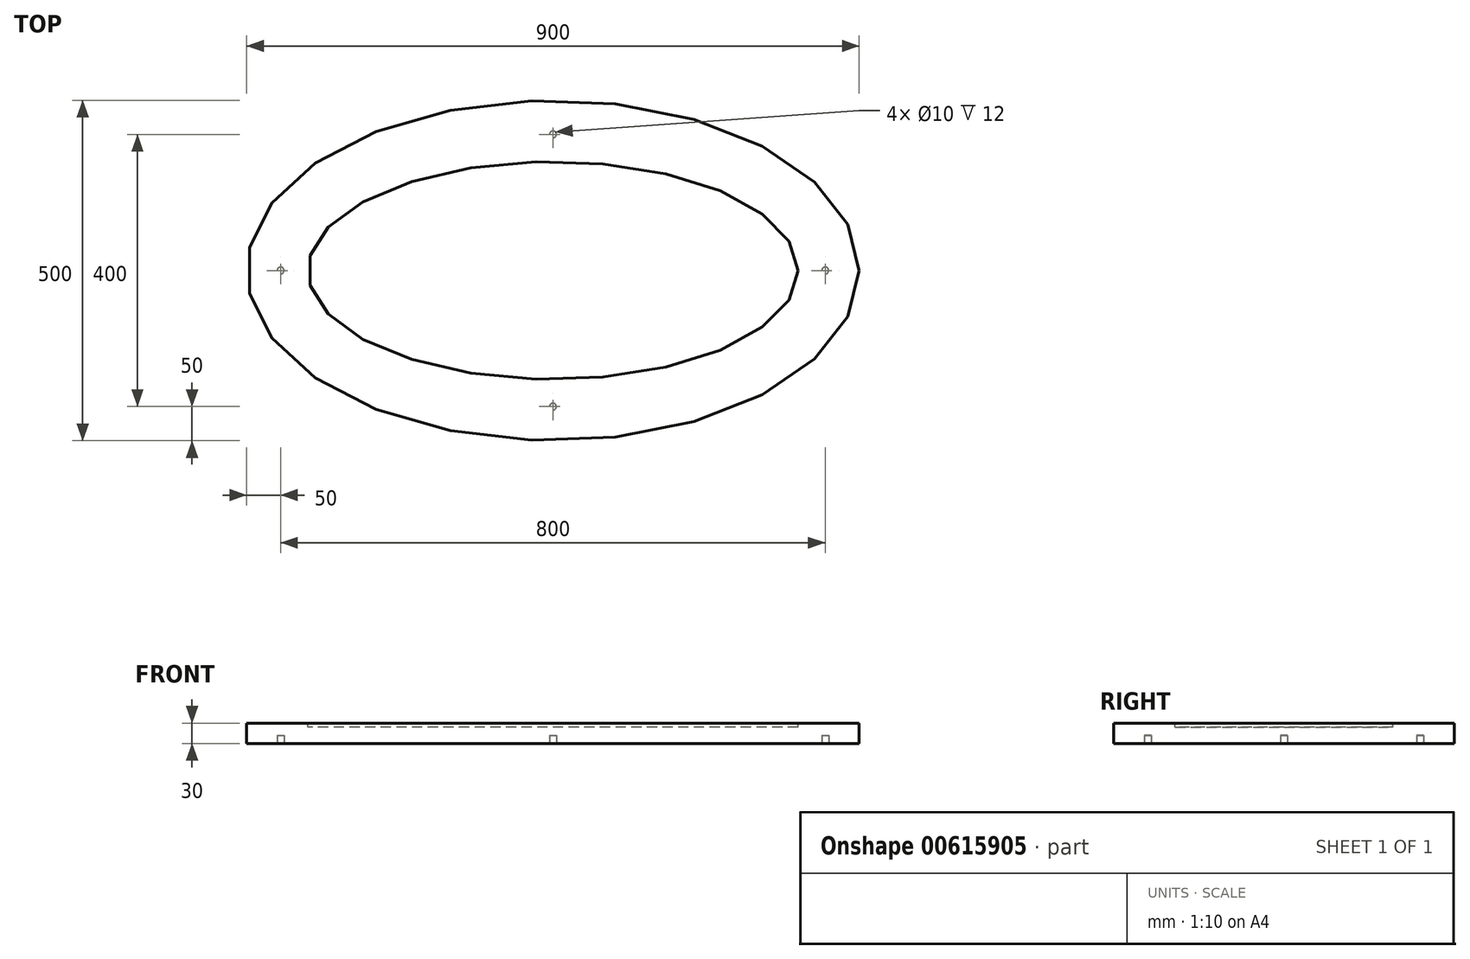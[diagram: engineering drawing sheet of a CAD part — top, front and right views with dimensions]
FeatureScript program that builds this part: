
annotation { "Feature Type Name" : "Feature", "Feature Type Description" : "" }
export const myFeature = defineFeature(function(context is Context, id is Id, definition is map)
    precondition{}
    {
        {
            var Q0;
            Q0=qCreatedBy(makeId("Top.planeOp"),FACE);
            var sketch = newSketch(context, id + "F0", { "sketchPlane" : qUnion([Q0])});
            skEllipse(sketch, "E0", {"center": v(0, 0) * mm, "majorRadius": 450 * mm, "minorRadius": 250 * mm, "majorAxis": v(1, 0)});
            skFitSpline(sketch, "E1.0", {"points": [v(349.97, -1.74) * mm, v(350.01, 0) * mm, v(349.97, 1.74) * mm, v(349.82, 4.08) * mm, v(349.42, 7.07) * mm, v(348.57, 10.9) * mm, v(347.27, 15.08) * mm, v(345.43, 19.64) * mm, v(342.94, 24.63) * mm, v(339.74, 30.04) * mm, v(335.72, 35.84) * mm, v(330.84, 41.98) * mm, v(325.03, 48.4) * mm, v(318.28, 55.05) * mm, v(310.55, 61.86) * mm, v(301.83, 68.75) * mm, v(293.75, 74.52) * mm, v(286.8, 79.12) * mm, v(281.33, 82.56) * mm, v(275.62, 85.98) * mm, v(269.67, 89.37) * mm, v(263.5, 92.72) * mm, v(257.12, 96) * mm, v(250.55, 99.23) * mm, v(241.54, 103.43) * mm, v(229.8, 108.51) * mm, v(215.03, 114.28) * mm, v(199.6, 119.7) * mm, v(178.22, 126.42) * mm, v(150.1, 133.81) * mm, v(120.4, 139.72) * mm, v(95.91, 143.5) * mm, v(77.2, 145.85) * mm, v(58.22, 147.69) * mm, v(42.2, 148.8) * mm, v(29.3, 149.42) * mm, v(19.56, 149.75) * mm, v(11.43, 149.92) * mm, v(4.9, 149.99) * mm, v(0, 150) * mm, v(-4.9, 149.99) * mm, v(-11.43, 149.92) * mm, v(-19.56, 149.75) * mm, v(-29.3, 149.42) * mm, v(-42.2, 148.8) * mm, v(-58.22, 147.69) * mm, v(-77.2, 145.85) * mm, v(-95.91, 143.5) * mm, v(-120.4, 139.72) * mm, v(-150.1, 133.81) * mm, v(-178.22, 126.42) * mm, v(-199.6, 119.7) * mm, v(-215.03, 114.28) * mm, v(-229.8, 108.51) * mm, v(-241.54, 103.43) * mm, v(-250.55, 99.23) * mm, v(-257.12, 96) * mm, v(-263.5, 92.72) * mm, v(-269.67, 89.37) * mm, v(-275.62, 85.98) * mm, v(-281.33, 82.56) * mm, v(-286.8, 79.12) * mm, v(-293.75, 74.52) * mm, v(-301.83, 68.75) * mm, v(-310.55, 61.86) * mm, v(-318.28, 55.05) * mm, v(-325.03, 48.4) * mm, v(-330.84, 41.98) * mm, v(-335.72, 35.84) * mm, v(-339.74, 30.04) * mm, v(-342.94, 24.63) * mm, v(-345.43, 19.64) * mm, v(-347.27, 15.08) * mm, v(-348.57, 10.9) * mm, v(-349.42, 7.07) * mm, v(-349.82, 4.08) * mm, v(-349.97, 1.74) * mm, v(-350.01, 0) * mm, v(-349.97, -1.74) * mm, v(-349.82, -4.08) * mm, v(-349.42, -7.07) * mm, v(-348.57, -10.9) * mm, v(-347.27, -15.08) * mm, v(-345.43, -19.64) * mm, v(-342.94, -24.63) * mm, v(-339.74, -30.04) * mm, v(-335.72, -35.84) * mm, v(-330.84, -41.98) * mm, v(-325.03, -48.4) * mm, v(-318.28, -55.05) * mm, v(-310.55, -61.86) * mm, v(-301.83, -68.75) * mm, v(-293.75, -74.52) * mm, v(-286.8, -79.12) * mm, v(-281.33, -82.56) * mm, v(-275.62, -85.98) * mm, v(-269.67, -89.37) * mm, v(-263.5, -92.72) * mm, v(-257.12, -96) * mm, v(-250.55, -99.23) * mm, v(-241.54, -103.43) * mm, v(-229.8, -108.51) * mm, v(-215.03, -114.28) * mm, v(-199.6, -119.7) * mm, v(-178.22, -126.42) * mm, v(-150.1, -133.81) * mm, v(-120.4, -139.72) * mm, v(-95.91, -143.5) * mm, v(-77.2, -145.85) * mm, v(-58.22, -147.69) * mm, v(-42.2, -148.8) * mm, v(-29.3, -149.42) * mm, v(-19.56, -149.75) * mm, v(-11.43, -149.92) * mm, v(-4.9, -149.99) * mm, v(0, -150) * mm, v(4.9, -149.99) * mm, v(11.43, -149.92) * mm, v(19.56, -149.75) * mm, v(29.3, -149.42) * mm, v(42.2, -148.8) * mm, v(58.22, -147.69) * mm, v(77.2, -145.85) * mm, v(95.91, -143.5) * mm, v(120.4, -139.72) * mm, v(150.1, -133.81) * mm, v(178.22, -126.42) * mm, v(199.6, -119.7) * mm, v(215.03, -114.28) * mm, v(229.8, -108.51) * mm, v(241.54, -103.43) * mm, v(250.55, -99.23) * mm, v(257.12, -96) * mm, v(263.5, -92.72) * mm, v(269.67, -89.37) * mm, v(275.62, -85.98) * mm, v(281.33, -82.56) * mm, v(286.8, -79.12) * mm, v(293.75, -74.52) * mm, v(301.83, -68.75) * mm, v(310.55, -61.86) * mm, v(318.28, -55.05) * mm, v(325.03, -48.4) * mm, v(330.84, -41.98) * mm, v(335.72, -35.84) * mm, v(339.74, -30.04) * mm, v(342.94, -24.63) * mm, v(345.43, -19.64) * mm, v(347.27, -15.08) * mm, v(348.57, -10.9) * mm, v(349.42, -7.07) * mm, v(349.82, -4.08) * mm, v(349.97, -1.74) * mm, v(350.01, 0) * mm, v(349.97, 1.74) * mm, v(349.97, -1.74) * mm]});
            skSolve(sketch);
        }
        {
            var Q0;
            Q0=makeQuery(id+"F0.imprint","IMPRINT",FACE,{"disambiguationData":[TD([[makeQuery(id+"F0.imprint","IMPRINT",EDGE,{"derivedFrom":sQuery(id+"F0.wireOp",EDGE,"E0")}),1.0]])]});
            extrude(context, id + "F1", {"entities" : qUnion([Q0]), "depth" : 30 * mm, "offsetDistance" : 25 * mm});
        }
        {
            var Q0;
            Q0=qCreatedBy(makeId("Top.planeOp"),FACE);
            cPlane(context, id + "F2", {"entities" : qUnion([Q0]), "cplaneType" : CPlaneType.OFFSET, "offset" : 30 * mm, "width" : 150 * mm, "height" : 150 * mm});
        }
        {
            var Q0;
            Q0=qCreatedBy(id+"F2.planeOp",FACE);
            var sketch = newSketch(context, id + "F3", { "sketchPlane" : qUnion([Q0])});
            skEllipse(sketch, "E2", {"center": v(0, 0) * mm, "majorRadius": 360 * mm, "minorRadius": 160 * mm, "majorAxis": v(1, 0)});
            skSolve(sketch);
        }
        {
            var Q0;
            Q0=qSketchRegion(id+"F3",true);
            extrude(context, id + "F4", {"entities" : qUnion([Q0]), "operationType" : NewBodyOperationType.REMOVE, "oppositeDirection" : true, "depth" : 6 * mm, "offsetDistance" : 25 * mm});
        }
        {
            var Q0;
            Q0=makeQuery(id+"F1.opExtrude","CAP_FACE",FACE,{"disambiguationData":[OSD([sQuery(id+"F0.wireOp",EDGE,"E0"),sQuery(id+"F0.wireOp",EDGE,"E1.0")])],"isStart":true});
            var sketch = newSketch(context, id + "F5", { "sketchPlane" : qUnion([Q0])});
            skLineSegment(sketch, "E3", {"start": v(0, 0) * mm, "end": v(0, 220.57) * mm, "construction": true});
            skLineSegment(sketch, "E4.0", {"start": v(-300, 0) * mm, "end": v(-300, 220.57) * mm, "construction": true});
            skFitSpline(sketch, "E5.0", {"points": [v(399.96, 3.31) * mm, v(400.03, 0) * mm, v(399.96, -3.31) * mm, v(399.8, -5.96) * mm, v(399.65, -7.95) * mm, v(399.45, -9.93) * mm, v(399.2, -11.93) * mm, v(398.92, -13.92) * mm, v(398.59, -15.91) * mm, v(398.2, -17.9) * mm, v(397.78, -19.91) * mm, v(397.3, -21.93) * mm, v(396.79, -23.94) * mm, v(396.22, -25.96) * mm, v(395.6, -27.99) * mm, v(394.95, -30.03) * mm, v(394.23, -32.07) * mm, v(393.47, -34.12) * mm, v(392.39, -36.87) * mm, v(390.32, -41.7) * mm, v(385.44, -51.48) * mm, v(376.28, -65.74) * mm, v(364.02, -80.2) * mm, v(352.3, -91.73) * mm, v(342.55, -100.3) * mm, v(331.84, -108.77) * mm, v(322.13, -115.7) * mm, v(313.89, -121.15) * mm, v(307.48, -125.19) * mm, v(300.83, -129.16) * mm, v(293.95, -133.08) * mm, v(286.86, -136.92) * mm, v(279.59, -140.67) * mm, v(272.14, -144.33) * mm, v(261.96, -149.08) * mm, v(248.82, -154.77) * mm, v(232.4, -161.18) * mm, v(215.37, -167.16) * mm, v(191.9, -174.53) * mm, v(161.29, -182.57) * mm, v(129.2, -188.96) * mm, v(102.82, -193.03) * mm, v(82.73, -195.55) * mm, v(62.36, -197.52) * mm, v(45.19, -198.7) * mm, v(31.36, -199.38) * mm, v(20.94, -199.74) * mm, v(12.23, -199.92) * mm, v(5.25, -199.99) * mm, v(0, -200) * mm, v(-5.25, -199.99) * mm, v(-12.23, -199.92) * mm, v(-20.94, -199.74) * mm, v(-31.36, -199.38) * mm, v(-45.19, -198.7) * mm, v(-62.36, -197.52) * mm, v(-82.73, -195.55) * mm, v(-102.82, -193.03) * mm, v(-129.2, -188.96) * mm, v(-161.29, -182.57) * mm, v(-191.9, -174.53) * mm, v(-215.37, -167.16) * mm, v(-232.4, -161.18) * mm, v(-248.82, -154.77) * mm, v(-261.96, -149.08) * mm, v(-272.14, -144.33) * mm, v(-279.59, -140.67) * mm, v(-286.86, -136.92) * mm, v(-293.95, -133.08) * mm, v(-300.83, -129.16) * mm, v(-307.48, -125.19) * mm, v(-313.89, -121.15) * mm, v(-322.13, -115.7) * mm, v(-331.84, -108.77) * mm, v(-342.55, -100.3) * mm, v(-352.3, -91.73) * mm, v(-364.02, -80.2) * mm, v(-376.28, -65.74) * mm, v(-385.44, -51.48) * mm, v(-390.32, -41.7) * mm, v(-392.39, -36.87) * mm, v(-393.47, -34.12) * mm, v(-394.23, -32.07) * mm, v(-394.95, -30.03) * mm, v(-395.6, -27.99) * mm, v(-396.22, -25.96) * mm, v(-396.79, -23.94) * mm, v(-397.3, -21.93) * mm, v(-397.78, -19.91) * mm, v(-398.2, -17.9) * mm, v(-398.59, -15.91) * mm, v(-398.92, -13.92) * mm, v(-399.2, -11.93) * mm, v(-399.45, -9.93) * mm, v(-399.65, -7.95) * mm, v(-399.8, -5.96) * mm, v(-399.96, -3.31) * mm, v(-400.03, 0) * mm, v(-399.96, 3.31) * mm, v(-399.8, 5.96) * mm, v(-399.65, 7.95) * mm, v(-399.45, 9.93) * mm, v(-399.2, 11.93) * mm, v(-398.92, 13.92) * mm, v(-398.59, 15.91) * mm, v(-398.2, 17.9) * mm, v(-397.78, 19.91) * mm, v(-397.3, 21.93) * mm, v(-396.79, 23.94) * mm, v(-396.22, 25.96) * mm, v(-395.6, 27.99) * mm, v(-394.95, 30.03) * mm, v(-394.23, 32.07) * mm, v(-393.47, 34.12) * mm, v(-392.39, 36.87) * mm, v(-390.32, 41.7) * mm, v(-385.44, 51.48) * mm, v(-376.28, 65.74) * mm, v(-364.02, 80.2) * mm, v(-352.3, 91.73) * mm, v(-342.55, 100.3) * mm, v(-331.84, 108.77) * mm, v(-322.13, 115.7) * mm, v(-313.89, 121.15) * mm, v(-307.48, 125.19) * mm, v(-300.83, 129.16) * mm, v(-293.95, 133.08) * mm, v(-286.86, 136.92) * mm, v(-279.59, 140.67) * mm, v(-272.14, 144.33) * mm, v(-261.96, 149.08) * mm, v(-248.82, 154.77) * mm, v(-232.4, 161.18) * mm, v(-215.37, 167.16) * mm, v(-191.9, 174.53) * mm, v(-161.29, 182.57) * mm, v(-129.2, 188.96) * mm, v(-102.82, 193.03) * mm, v(-82.73, 195.55) * mm, v(-62.36, 197.52) * mm, v(-45.19, 198.7) * mm, v(-31.36, 199.38) * mm, v(-20.94, 199.74) * mm, v(-12.23, 199.92) * mm, v(-5.25, 199.99) * mm, v(0, 200) * mm, v(5.25, 199.99) * mm, v(12.23, 199.92) * mm, v(20.94, 199.74) * mm, v(31.36, 199.38) * mm, v(45.19, 198.7) * mm, v(62.36, 197.52) * mm, v(82.73, 195.55) * mm, v(102.82, 193.03) * mm, v(129.2, 188.96) * mm, v(161.29, 182.57) * mm, v(191.9, 174.53) * mm, v(215.37, 167.16) * mm, v(232.4, 161.18) * mm, v(248.82, 154.77) * mm, v(261.96, 149.08) * mm, v(272.14, 144.33) * mm, v(279.59, 140.67) * mm, v(286.86, 136.92) * mm, v(293.95, 133.08) * mm, v(300.83, 129.16) * mm, v(307.48, 125.19) * mm, v(313.89, 121.15) * mm, v(322.13, 115.7) * mm, v(331.84, 108.77) * mm, v(342.55, 100.3) * mm, v(352.3, 91.73) * mm, v(364.02, 80.2) * mm, v(376.28, 65.74) * mm, v(385.44, 51.48) * mm, v(390.32, 41.7) * mm, v(392.39, 36.87) * mm, v(393.47, 34.12) * mm, v(394.23, 32.07) * mm, v(394.95, 30.03) * mm, v(395.6, 27.99) * mm, v(396.22, 25.96) * mm, v(396.79, 23.94) * mm, v(397.3, 21.93) * mm, v(397.78, 19.91) * mm, v(398.2, 17.9) * mm, v(398.59, 15.91) * mm, v(398.92, 13.92) * mm, v(399.2, 11.93) * mm, v(399.45, 9.93) * mm, v(399.65, 7.95) * mm, v(399.8, 5.96) * mm, v(399.96, 3.31) * mm, v(400.03, 0) * mm, v(399.96, -3.31) * mm, v(399.96, 3.31) * mm], "construction": true});
            skFitSpline(sketch, "E6.0", {"points": [v(444.91, -5.99) * mm, v(445.04, 0) * mm, v(444.91, 5.99) * mm, v(444.38, 13.94) * mm, v(443.05, 23.84) * mm, v(440.41, 35.64) * mm, v(435.51, 51.22) * mm, v(426.83, 70.41) * mm, v(412.4, 92.81) * mm, v(397.08, 110.82) * mm, v(382.92, 124.74) * mm, v(371.35, 134.9) * mm, v(358.85, 144.79) * mm, v(347.67, 152.76) * mm, v(338.28, 158.97) * mm, v(331, 163.55) * mm, v(324.76, 167.28) * mm, v(319.66, 170.23) * mm, v(315.78, 172.41) * mm, v(311.85, 174.57) * mm, v(306.54, 177.4) * mm, v(299.8, 180.88) * mm, v(291.56, 184.93) * mm, v(280.34, 190.16) * mm, v(265.92, 196.4) * mm, v(248.02, 203.4) * mm, v(229.55, 209.88) * mm, v(204.23, 217.83) * mm, v(171.36, 226.46) * mm, v(137.12, 233.27) * mm, v(109.05, 237.6) * mm, v(87.7, 240.28) * mm, v(66.07, 242.38) * mm, v(47.87, 243.63) * mm, v(33.22, 244.34) * mm, v(22.18, 244.72) * mm, v(12.96, 244.91) * mm, v(5.56, 244.99) * mm, v(0, 245) * mm, v(-5.56, 244.99) * mm, v(-12.96, 244.91) * mm, v(-22.18, 244.72) * mm, v(-33.22, 244.34) * mm, v(-47.87, 243.63) * mm, v(-66.07, 242.38) * mm, v(-87.7, 240.28) * mm, v(-109.05, 237.6) * mm, v(-137.12, 233.27) * mm, v(-171.36, 226.46) * mm, v(-204.23, 217.83) * mm, v(-229.55, 209.88) * mm, v(-248.02, 203.4) * mm, v(-265.92, 196.4) * mm, v(-280.34, 190.16) * mm, v(-291.56, 184.93) * mm, v(-299.8, 180.88) * mm, v(-306.54, 177.4) * mm, v(-311.85, 174.57) * mm, v(-315.78, 172.41) * mm, v(-319.66, 170.23) * mm, v(-324.76, 167.28) * mm, v(-331, 163.55) * mm, v(-338.28, 158.97) * mm, v(-347.67, 152.76) * mm, v(-358.85, 144.79) * mm, v(-371.35, 134.9) * mm, v(-382.92, 124.74) * mm, v(-397.08, 110.82) * mm, v(-412.4, 92.81) * mm, v(-426.83, 70.41) * mm, v(-435.51, 51.22) * mm, v(-440.41, 35.64) * mm, v(-443.05, 23.84) * mm, v(-444.38, 13.94) * mm, v(-444.91, 5.99) * mm, v(-445.04, 0) * mm, v(-444.91, -5.99) * mm, v(-444.38, -13.94) * mm, v(-443.05, -23.84) * mm, v(-440.41, -35.64) * mm, v(-435.51, -51.22) * mm, v(-426.83, -70.41) * mm, v(-412.4, -92.81) * mm, v(-397.08, -110.82) * mm, v(-382.92, -124.74) * mm, v(-371.35, -134.9) * mm, v(-358.85, -144.79) * mm, v(-347.67, -152.76) * mm, v(-338.28, -158.97) * mm, v(-331, -163.55) * mm, v(-324.76, -167.28) * mm, v(-319.66, -170.23) * mm, v(-315.78, -172.41) * mm, v(-311.85, -174.57) * mm, v(-306.54, -177.4) * mm, v(-299.8, -180.88) * mm, v(-291.56, -184.93) * mm, v(-280.34, -190.16) * mm, v(-265.92, -196.4) * mm, v(-248.02, -203.4) * mm, v(-229.55, -209.88) * mm, v(-204.23, -217.83) * mm, v(-171.36, -226.46) * mm, v(-137.12, -233.27) * mm, v(-109.05, -237.6) * mm, v(-87.7, -240.28) * mm, v(-66.07, -242.38) * mm, v(-47.87, -243.63) * mm, v(-33.22, -244.34) * mm, v(-22.18, -244.72) * mm, v(-12.96, -244.91) * mm, v(-5.56, -244.99) * mm, v(0, -245) * mm, v(5.56, -244.99) * mm, v(12.96, -244.91) * mm, v(22.18, -244.72) * mm, v(33.22, -244.34) * mm, v(47.87, -243.63) * mm, v(66.07, -242.38) * mm, v(87.7, -240.28) * mm, v(109.05, -237.6) * mm, v(137.12, -233.27) * mm, v(171.36, -226.46) * mm, v(204.23, -217.83) * mm, v(229.55, -209.88) * mm, v(248.02, -203.4) * mm, v(265.92, -196.4) * mm, v(280.34, -190.16) * mm, v(291.56, -184.93) * mm, v(299.8, -180.88) * mm, v(306.54, -177.4) * mm, v(311.85, -174.57) * mm, v(315.78, -172.41) * mm, v(319.66, -170.23) * mm, v(324.76, -167.28) * mm, v(331, -163.55) * mm, v(338.28, -158.97) * mm, v(347.67, -152.76) * mm, v(358.85, -144.79) * mm, v(371.35, -134.9) * mm, v(382.92, -124.74) * mm, v(397.08, -110.82) * mm, v(412.4, -92.81) * mm, v(426.83, -70.41) * mm, v(435.51, -51.22) * mm, v(440.41, -35.64) * mm, v(443.05, -23.84) * mm, v(444.38, -13.94) * mm, v(444.91, -5.99) * mm, v(445.04, 0) * mm, v(444.91, 5.99) * mm, v(444.91, -5.99) * mm], "construction": true});
            skLineSegment(sketch, "E7", {"start": v(0, 0) * mm, "end": v(0, -277.53) * mm, "construction": true});
            skLineSegment(sketch, "E8", {"start": v(0, 0) * mm, "end": v(560.25, 0) * mm, "construction": true});
            skCircle(sketch, "E9", {"center": v(0, -200) * mm, "radius": 5 * mm});
            skCircle(sketch, "E10.MirrorC", {"center": v(0, 200) * mm, "radius": 5 * mm});
            skCircle(sketch, "E11", {"center": v(400, 0) * mm, "radius": 5 * mm});
            skCircle(sketch, "E12.MirrorC", {"center": v(-400, 0) * mm, "radius": 5 * mm});
            skSolve(sketch);
        }
        {
            var Q0;
            Q0=qSketchRegion(id+"F5",true);
            extrude(context, id + "F6", {"entities" : qUnion([Q0]), "operationType" : NewBodyOperationType.REMOVE, "oppositeDirection" : true, "depth" : 12 * mm, "offsetDistance" : 25 * mm});
        }
    });
